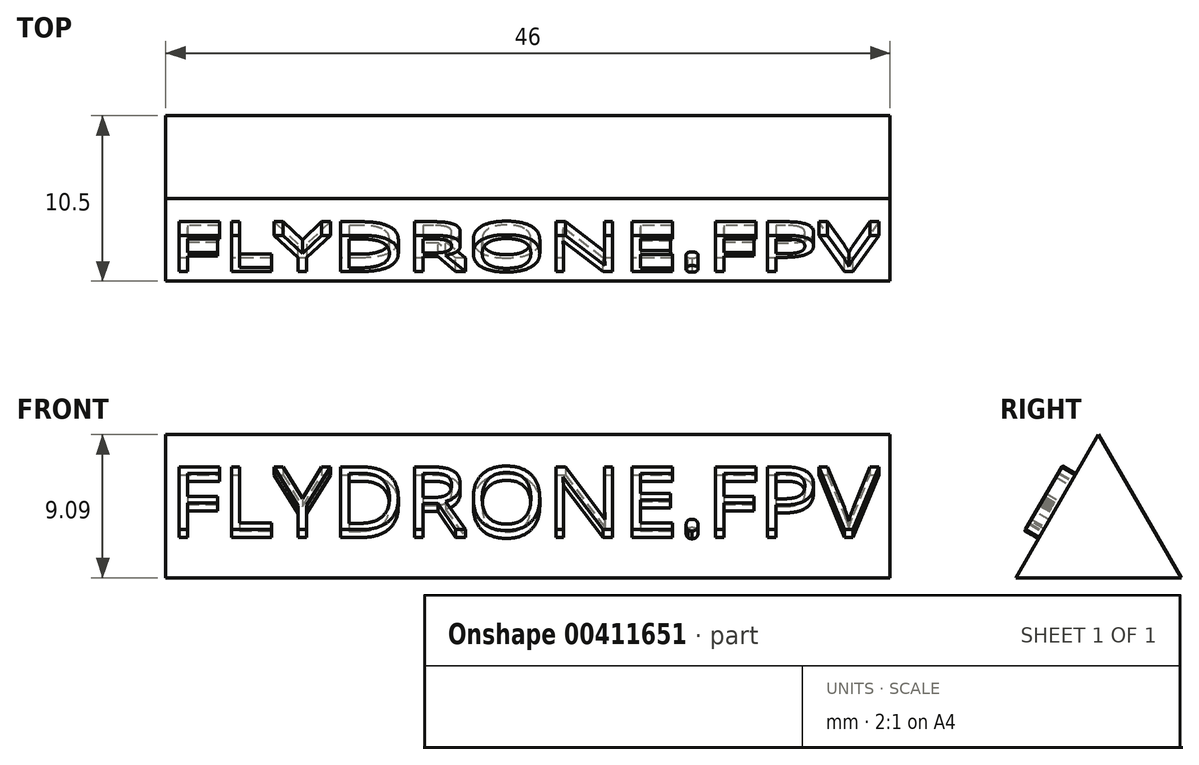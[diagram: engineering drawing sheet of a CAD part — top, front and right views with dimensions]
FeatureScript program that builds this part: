
annotation { "Feature Type Name" : "Feature", "Feature Type Description" : "" }
export const myFeature = defineFeature(function(context is Context, id is Id, definition is map)
    precondition{}
    {
        {
            var Q0;
            Q0=qCreatedBy(makeId("Right.planeOp"),FACE);
            var sketch = newSketch(context, id + "F0", { "sketchPlane" : qUnion([Q0])});
            skCircle(sketch, "E0", {"center": v(0, 0) * mm, "radius": 6.06 * mm, "construction": true});
            skLineSegment(sketch, "E1", {"start": v(0, 6.06) * mm, "end": v(0, 0) * mm, "construction": true});
            skLineSegment(sketch, "E2", {"start": v(0, 0) * mm, "end": v(-6.74, -3.9) * mm, "construction": true});
            skLineSegment(sketch, "E3", {"start": v(0, 0) * mm, "end": v(7.07, -4.08) * mm, "construction": true});
            skLineSegment(sketch, "E4", {"start": v(-5.25, -3.03) * mm, "end": v(5.25, -3.03) * mm});
            skLineSegment(sketch, "E5", {"start": v(-5.25, -3.03) * mm, "end": v(0, 6.06) * mm});
            skLineSegment(sketch, "E6", {"start": v(0, 6.06) * mm, "end": v(5.25, -3.03) * mm});
            skSolve(sketch);
        }
        {
            var Q0;
            Q0=makeQuery(id+"F0.imprint","IMPRINT",FACE,{"disambiguationData":[TD([[makeQuery(id+"F0.imprint","IMPRINT",EDGE,{"derivedFrom":sQuery(id+"F0.wireOp",EDGE,"E4")}),1.0]])]});
            extrude(context, id + "F1", {"entities" : qUnion([Q0]), "depth" : 46 * mm});
        }
        {
            var Q0;
            Q0=makeQuery(id+"F1.opExtrude","SWEPT_FACE",FACE,{"disambiguationData":[OSD([sQuery(id+"F0.wireOp",EDGE,"E5")])]});
            var sketch = newSketch(context, id + "F2", { "sketchPlane" : qUnion([Q0])});
            skText(sketch, "E7", { "text": "FLYDRONE.FPV", "fontName": "OpenSans-Regular.ttf"});
            const initialGuessF2  = {"E7": [0.00022, -0.0023, 1, 0, 0.00463]};
            skSetInitialGuess(sketch, initialGuessF2);
            skSolve(sketch);
        }
        {
            var Q0;
            Q0 = qSketchRegion(id + "F2", true);
            extrude(context, id + "F3", {"entities" : qUnion([Q0]), "operationType" : NewBodyOperationType.ADD, "depth" : 1 * mm});
        }
    });
